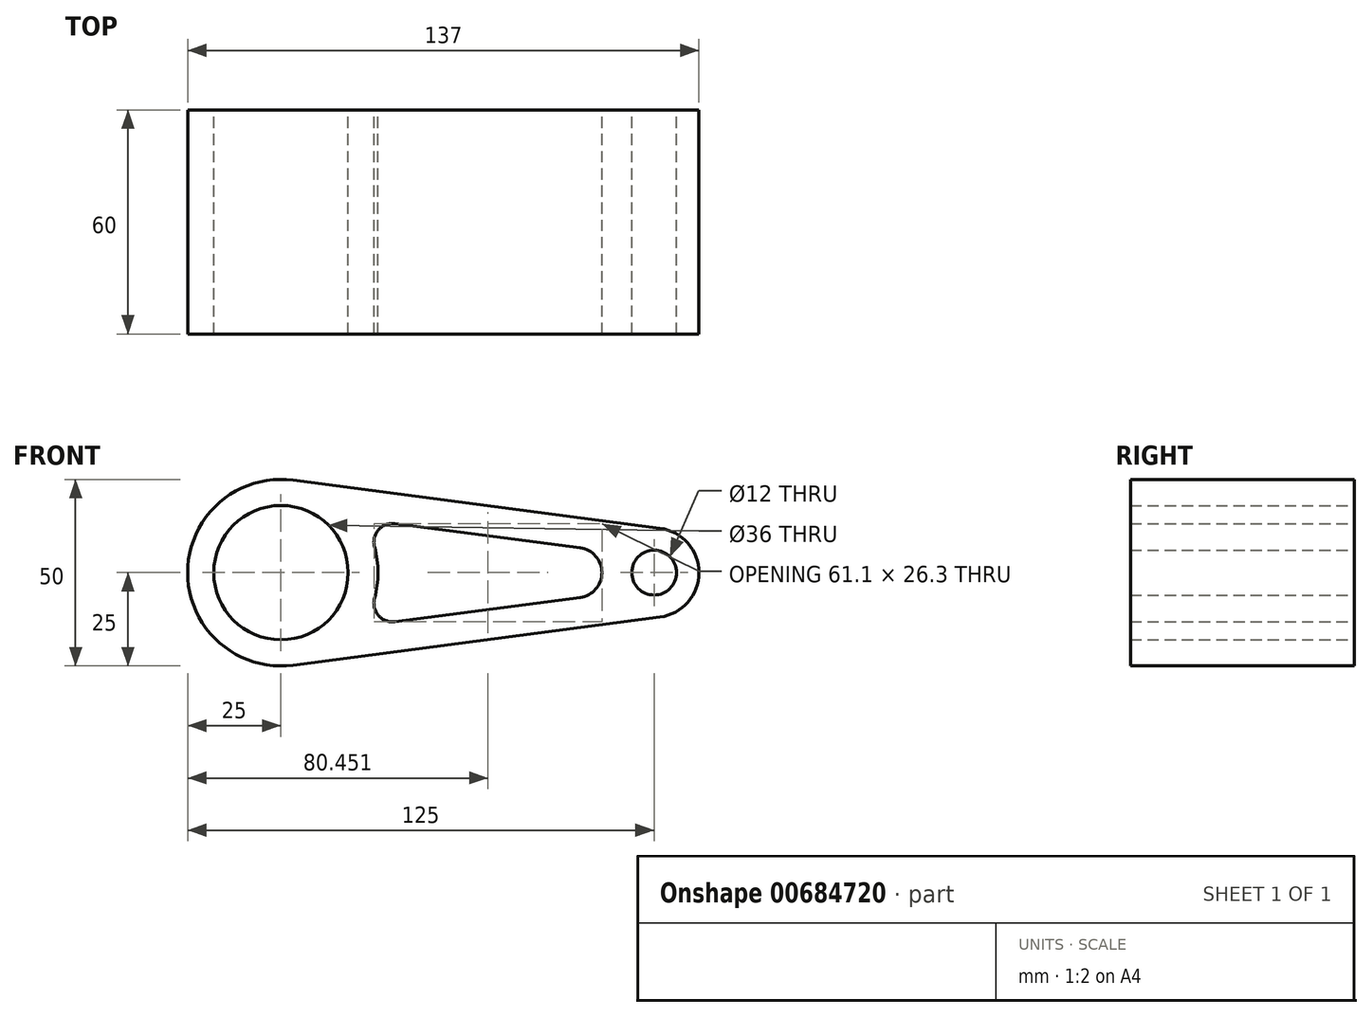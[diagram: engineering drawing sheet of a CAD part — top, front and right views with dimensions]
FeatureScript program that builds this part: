
annotation { "Feature Type Name" : "Feature", "Feature Type Description" : "" }
export const myFeature = defineFeature(function(context is Context, id is Id, definition is map)
    precondition{}
    {
        {
            var Q0;
            Q0=qCreatedBy(makeId("Front.planeOp"),FACE);
            var sketch = newSketch(context, id + "F0", { "sketchPlane" : qUnion([Q0])});
            skLineSegment(sketch, "E0", {"start": v(101.56, -11.9) * mm, "end": v(3.25, -24.79) * mm});
            skArc(sketch, "E1", {"start": v(3.25, 24.79) * mm, "mid": v(-25, 0) * mm, "end": v(3.25, -24.79) * mm});
            skCircle(sketch, "E2", {"center": v(0, 0) * mm, "radius": 18 * mm});
            skCircle(sketch, "E3", {"center": v(100, 0) * mm, "radius": 6 * mm});
            skArc(sketch, "E4", {"start": v(30.55, 13.14) * mm, "mid": v(26.13, 11.47) * mm, "end": v(25.08, 6.86) * mm});
            skArc(sketch, "E5", {"start": v(25.08, -6.86) * mm, "mid": v(26, 0) * mm, "end": v(25.08, 6.86) * mm});
            skArc(sketch, "E6", {"start": v(25.08, -6.86) * mm, "mid": v(26.13, -11.47) * mm, "end": v(30.55, -13.14) * mm});
            skArc(sketch, "E7", {"start": v(80.18, -6.63) * mm, "mid": v(86, 0) * mm, "end": v(80.18, 6.63) * mm});
            skLineSegment(sketch, "E8", {"start": v(30.55, 13.14) * mm, "end": v(80.18, 6.63) * mm});
            skLineSegment(sketch, "E9", {"start": v(30.55, -13.14) * mm, "end": v(80.18, -6.63) * mm});
            skLineSegment(sketch, "E10", {"start": v(3.25, 24.79) * mm, "end": v(101.56, 11.9) * mm});
            skArc(sketch, "E11", {"start": v(101.56, -11.9) * mm, "mid": v(112, 0) * mm, "end": v(101.56, 11.9) * mm});
            skSolve(sketch);
        }
        {
            var Q0;
            Q0 = qSketchRegion(id + "F0", true);
            extrude(context, id + "F1", {"entities" : qUnion([Q0]), "endBound" : BoundingType.SYMMETRIC, "depth" : 60 * mm, "offsetDistance" : 25.4 * mm});
        }
    });
